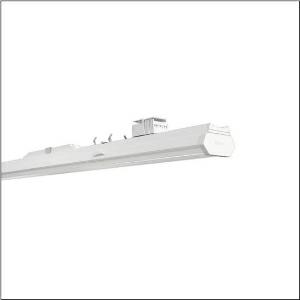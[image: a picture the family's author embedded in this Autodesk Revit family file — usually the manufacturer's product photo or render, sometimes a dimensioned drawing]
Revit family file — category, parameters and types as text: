
# Revit family: licross_r__11_protected_mo_51td11cn49xg_045e
name_source: partatom
category: Lighting Fixtures
units: mm (PartAtom-declared; Revit-internal decimal feet)

## family parameters
Cut with Voids When Loaded = No
Host = Face
Light Source = No
Part Type = Normal
Room Calculation Point = No
Round Connector Dimension = Use Diameter
Shared = No

## types (1)
- --- (1 x LED, 9030 lm, 49.4 W, 4000K)
    Apparent Load = 49 VA
    CIE Flux Codes = 83 94 98 100 100
    Color Rendering = 80
    Color Temperature = 4000K
    Default Elevation = 1800 mm
    Description = Licross® 11 Protected MO, luminaire insert, of sheet steel, galvanised, coil coated, white, length: 1.500mm, width: 90mm, height: 101mm, LED rated luminous flux: 9.030lm, light colour: 840, control gear: ON/OFF Multilumen, CLOi, with plug, 3-pole, with phase selection, mains connection: 220..240V, AC, 50/60Hz, halogen-free wiring, primary light control with lens, of plastic, primary optical cover: cover, of PMMA, light emission: direct with ceiling illumination distribution, primary light characteristic: symmetric, protection rating (complete): IP54, insulation class (complete): insulation class I (protective earthing), certification: CE, ENEC, VDE, UKCA, protection symbol: D if used in an environment with non-conductive dust loads with corresponding accessories, impact resistance: IK06, permissible ambient temperature for indoor applications: -35..+40°C, corresponds to IFS (International Featured Standards) requirements for safety and quality in the food industry, reducing of maximum allowable ambient temperature of 5°C with ceiling mounting, LABS conformity tested according to VDMA 24364:2018-05, packaging unit: 1 piece
    Height = 92 mm
    Lamp = 1 x LED
    Lamp Light Flux = 9030 lm
    Lamp Power = 49.4 W
    Lamp count = 1
    Length = 1500 mm
    Luminous efficacy = 183 lm/W
    Manufacturer = Siteco
    ModVariant = No
    Model = 51TD11CN49XG
    Mounting Place = Ceiling
    Mounting Type = Pendant
    Number of Poles = 1
    OnlyDefault = Yes
    Power Factor = 1
    Product Name = Licross® 11 Protected MO
    Product group = luminaire insert
    ProductGroupID = 902
    Protection Class = Protection class I
    Protection Degree = IP 54
    RLX_Detail_Level = 1
    RlxData = <blob elided: 21845 chars, md5=c2fac80c>
    Socket = socket
    Standby Power = 0 W
    System Light Flux = 9030 lm
    System Power = 49 W
    Type Comments = factory setting: luminous flux: 100 % | (A | C | E) | 113 mA
    Type Image = l_1256145.jpg
    URL = http://relux.com
    VarID = @adj_003703
    Voltage = 0 V
    Weight = 0.00 kg
    Width = 88 mm

## geometry (parser evidence)
native form markers: Blend x4, Sweep x11
no freeform markers — native parametric forms only
